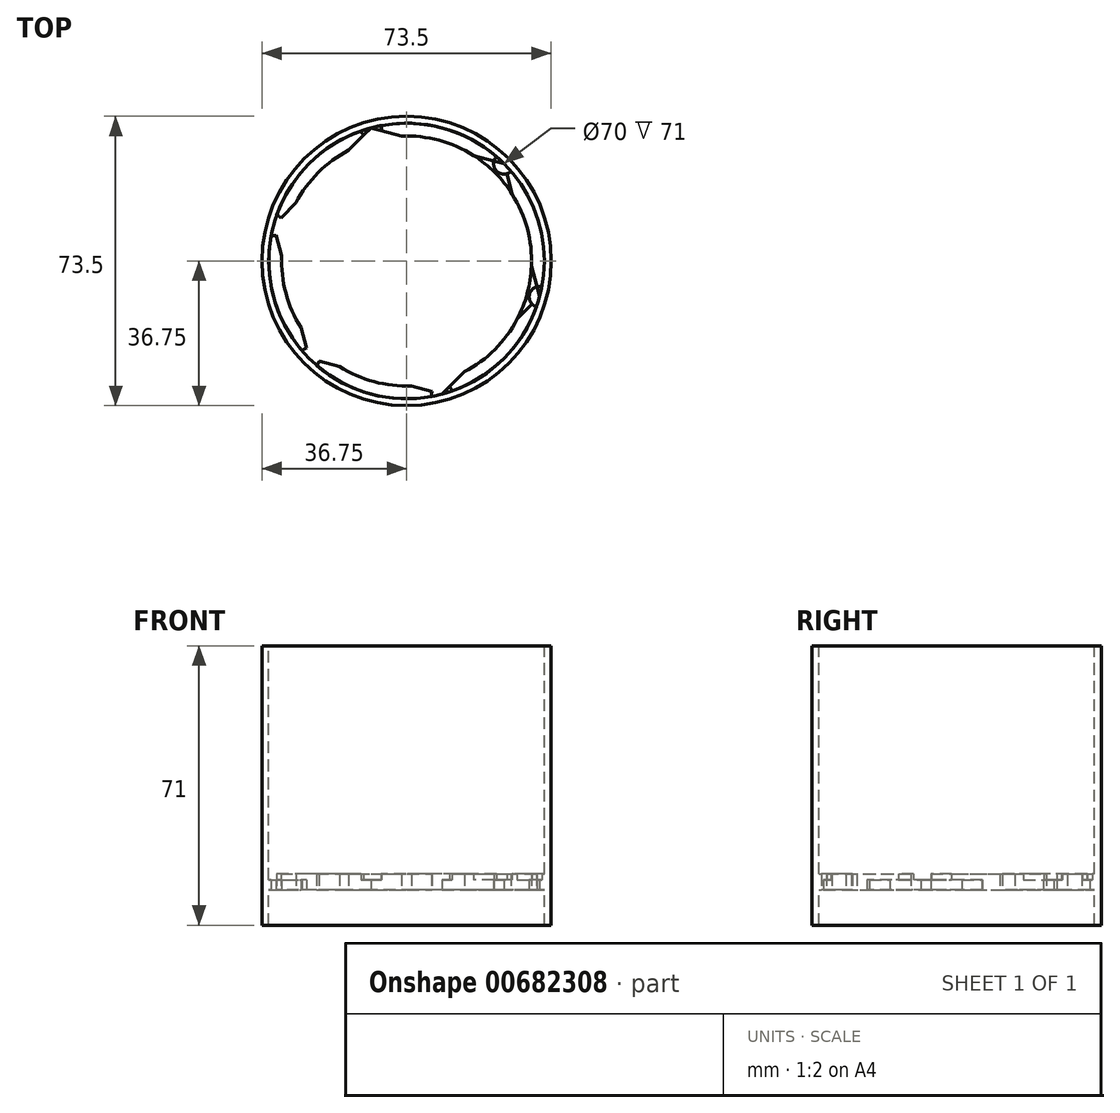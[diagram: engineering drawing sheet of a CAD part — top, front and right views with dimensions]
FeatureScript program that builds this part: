
annotation { "Feature Type Name" : "Feature", "Feature Type Description" : "" }
export const myFeature = defineFeature(function(context is Context, id is Id, definition is map)
    precondition{}
    {
        {
            var Q0;
            Q0=qCreatedBy(makeId("Top.planeOp"),FACE);
            var sketch = newSketch(context, id + "F0", { "sketchPlane" : qUnion([Q0])});
            skCircle(sketch, "E0", {"center": v(0, 0) * mm, "radius": 35 * mm});
            skCircle(sketch, "E1", {"center": v(0, 0) * mm, "radius": 36.75 * mm});
            skCircle(sketch, "E2", {"center": v(0, 0) * mm, "radius": 31.75 * mm});
            skCircle(sketch, "E3.cCircle", {"center": v(0, 0) * mm, "radius": 35 * mm, "construction": true});
            skLineSegment(sketch, "E3.0", {"start": v(-33.8, 9.1) * mm, "end": v(-9.02, 33.82) * mm});
            skLineSegment(sketch, "E3.1", {"start": v(-9.02, 33.82) * mm, "end": v(24.77, 24.72) * mm});
            skLineSegment(sketch, "E3.2", {"start": v(24.77, 24.72) * mm, "end": v(33.8, -9.1) * mm});
            skLineSegment(sketch, "E3.3", {"start": v(33.8, -9.1) * mm, "end": v(9.02, -33.82) * mm});
            skLineSegment(sketch, "E3.4", {"start": v(9.02, -33.82) * mm, "end": v(-24.77, -24.72) * mm});
            skLineSegment(sketch, "E3.5", {"start": v(-24.77, -24.72) * mm, "end": v(-33.8, 9.1) * mm});
            skArc(sketch, "E4", {"start": v(-6.44, 34.4) * mm, "mid": v(-8.34, 31.26) * mm, "end": v(-11.56, 33.04) * mm});
            skArc(sketch, "E5", {"start": v(26.57, 22.78) * mm, "mid": v(22.9, 22.85) * mm, "end": v(22.83, 26.53) * mm});
            skArc(sketch, "E6", {"start": v(33.01, -11.62) * mm, "mid": v(31.24, -8.4) * mm, "end": v(34.39, -6.5) * mm});
            skArc(sketch, "E7", {"start": v(6.44, -34.4) * mm, "mid": v(8.34, -31.26) * mm, "end": v(11.56, -33.04) * mm});
            skArc(sketch, "E8", {"start": v(-26.57, -22.78) * mm, "mid": v(-22.9, -22.85) * mm, "end": v(-22.83, -26.53) * mm});
            skArc(sketch, "E9", {"start": v(-33.01, 11.62) * mm, "mid": v(-31.24, 8.4) * mm, "end": v(-34.39, 6.5) * mm});
            skSolve(sketch);
        }
        {
            var Q0;
            Q0=makeQuery(id+"F0.imprint","IMPRINT",FACE,{"disambiguationData":[TD([[makeQuery(id+"F0.imprint","IMPRINT",EDGE,{"derivedFrom":sQuery(id+"F0.wireOp",EDGE,"E1")}),1.0]])]});
            extrude(context, id + "F1", {"entities" : qUnion([Q0]), "oppositeDirection" : true, "depth" : 9 * mm, "offsetDistance" : 25 * mm});
        }
        {
            var Q0;
            Q0=makeQuery(id+"F0.imprint","IMPRINT",FACE,{"disambiguationData":[TD([[makeQuery(id+"F0.imprint","IMPRINT",EDGE,{"derivedFrom":sQuery(id+"F0.wireOp",EDGE,"E1")}),1.0]])]});
            extrude(context, id + "F2", {"entities" : qUnion([Q0]), "operationType" : NewBodyOperationType.ADD, "depth" : 62 * mm, "offsetDistance" : 25 * mm});
        }
        {
            var Q0;
            {var subQ5=sQuery(id+"F0.wireOp",EDGE,"E0");var subQ8=sQuery(id+"F0.wireOp",EDGE,"E4");var subQ10=makeQuery(id+"F0.imprint","INTERSECT",VERTEX,{"disambiguationData":[OD(1.0)],"derivedFrom":[subQ5,subQ8]});Q0=makeQuery(id+"F0.imprint","IMPRINT",FACE,{"disambiguationData":[TD([[makeQuery(id+"F0.imprint","IMPRINT",EDGE,{"disambiguationData":[TD([[subQ10,-1.0]])],"derivedFrom":subQ5}),1.0]])]});}
            var Q1;
            {var subQ0=sQuery(id+"F0.wireOp",EDGE,"E3.0");var subQ1=sQuery(id+"F0.wireOp",EDGE,"E2");var subQ2=makeQuery(id+"F0.imprint","INTERSECT",VERTEX,{"disambiguationData":[OD(1.0)],"derivedFrom":[subQ1,subQ0]});Q1=makeQuery(id+"F0.imprint","IMPRINT",FACE,{"disambiguationData":[TD([[makeQuery(id+"F0.imprint","IMPRINT",EDGE,{"disambiguationData":[TD([[subQ2,-1.0]])],"derivedFrom":subQ1}),-1.0]])]});}
            var Q2;
            {var subQ6=sQuery(id+"F0.wireOp",EDGE,"E8");var subQ8=sQuery(id+"F0.wireOp",EDGE,"E0");var subQ9=makeQuery(id+"F0.imprint","INTERSECT",VERTEX,{"disambiguationData":[OD(0.0)],"derivedFrom":[subQ8,subQ6]});Q2=makeQuery(id+"F0.imprint","IMPRINT",FACE,{"disambiguationData":[TD([[makeQuery(id+"F0.imprint","IMPRINT",EDGE,{"disambiguationData":[TD([[subQ9,1.0]])],"derivedFrom":subQ8}),1.0]])]});}
            var Q3;
            {var subQ1=sQuery(id+"F0.wireOp",EDGE,"E3.0");var subQ3=sQuery(id+"F0.wireOp",EDGE,"E9");var subQ4=makeQuery(id+"F0.imprint","INTERSECT",VERTEX,{"derivedFrom":[subQ1,subQ3]});Q3=makeQuery(id+"F0.imprint","IMPRINT",FACE,{"disambiguationData":[TD([[makeQuery(id+"F0.imprint","IMPRINT",EDGE,{"disambiguationData":[TD([[subQ4,-1.0]])],"derivedFrom":subQ3}),-1.0]])]});}
            var Q4;
            {var subQ1=sQuery(id+"F0.wireOp",EDGE,"E0");var subQ3=sQuery(id+"F0.wireOp",EDGE,"E9");var subQ4=makeQuery(id+"F0.imprint","INTERSECT",VERTEX,{"disambiguationData":[OD(0.0)],"derivedFrom":[subQ1,subQ3]});Q4=makeQuery(id+"F0.imprint","IMPRINT",FACE,{"disambiguationData":[TD([[makeQuery(id+"F0.imprint","IMPRINT",EDGE,{"disambiguationData":[TD([[subQ4,-1.0]])],"derivedFrom":subQ3}),-1.0]])]});}
            var Q5;
            {var subQ1=sQuery(id+"F0.wireOp",EDGE,"E0");var subQ3=sQuery(id+"F0.wireOp",EDGE,"E9");var subQ4=makeQuery(id+"F0.imprint","INTERSECT",VERTEX,{"disambiguationData":[OD(1.0)],"derivedFrom":[subQ1,subQ3]});Q5=makeQuery(id+"F0.imprint","IMPRINT",FACE,{"disambiguationData":[TD([[makeQuery(id+"F0.imprint","IMPRINT",EDGE,{"disambiguationData":[TD([[subQ4,1.0]])],"derivedFrom":subQ3}),-1.0]])]});}
            var Q6;
            {var subQ0=sQuery(id+"F0.wireOp",EDGE,"E3.5");var subQ1=sQuery(id+"F0.wireOp",EDGE,"E2");var subQ2=makeQuery(id+"F0.imprint","INTERSECT",VERTEX,{"disambiguationData":[OD(1.0)],"derivedFrom":[subQ1,subQ0]});Q6=makeQuery(id+"F0.imprint","IMPRINT",FACE,{"disambiguationData":[TD([[makeQuery(id+"F0.imprint","IMPRINT",EDGE,{"disambiguationData":[TD([[subQ2,-1.0]])],"derivedFrom":subQ1}),-1.0]])]});}
            var Q7;
            Q7=makeQuery(id+"F0.imprint","IMPRINT",FACE,{"disambiguationData":[TD([[makeQuery(id+"F0.imprint","IMPRINT",EDGE,{"derivedFrom":sQuery(id+"F0.wireOp",EDGE,"yZACQcL7-3FR9-Hpo4-Rt52-3T5EJ3K1hziJ")}),-1.0]])]});
            var Q8;
            {var subQ5=sQuery(id+"F0.wireOp",EDGE,"E7");var subQ6=sQuery(id+"F0.wireOp",EDGE,"E0");var subQ7=makeQuery(id+"F0.imprint","INTERSECT",VERTEX,{"disambiguationData":[OD(0.0)],"derivedFrom":[subQ6,subQ5]});Q8=makeQuery(id+"F0.imprint","IMPRINT",FACE,{"disambiguationData":[TD([[makeQuery(id+"F0.imprint","IMPRINT",EDGE,{"disambiguationData":[TD([[subQ7,1.0]])],"derivedFrom":subQ6}),1.0]])]});}
            var Q9;
            {var subQ1=sQuery(id+"F0.wireOp",EDGE,"E3.4");var subQ3=sQuery(id+"F0.wireOp",EDGE,"E8");var subQ4=makeQuery(id+"F0.imprint","INTERSECT",VERTEX,{"derivedFrom":[subQ1,subQ3]});Q9=makeQuery(id+"F0.imprint","IMPRINT",FACE,{"disambiguationData":[TD([[makeQuery(id+"F0.imprint","IMPRINT",EDGE,{"disambiguationData":[TD([[subQ4,1.0]])],"derivedFrom":subQ3}),-1.0]])]});}
            var Q10;
            {var subQ1=sQuery(id+"F0.wireOp",EDGE,"E0");var subQ3=sQuery(id+"F0.wireOp",EDGE,"E8");var subQ4=makeQuery(id+"F0.imprint","INTERSECT",VERTEX,{"disambiguationData":[OD(1.0)],"derivedFrom":[subQ1,subQ3]});Q10=makeQuery(id+"F0.imprint","IMPRINT",FACE,{"disambiguationData":[TD([[makeQuery(id+"F0.imprint","IMPRINT",EDGE,{"disambiguationData":[TD([[subQ4,1.0]])],"derivedFrom":subQ3}),-1.0]])]});}
            var Q11;
            {var subQ1=sQuery(id+"F0.wireOp",EDGE,"E0");var subQ3=sQuery(id+"F0.wireOp",EDGE,"E8");var subQ4=makeQuery(id+"F0.imprint","INTERSECT",VERTEX,{"disambiguationData":[OD(0.0)],"derivedFrom":[subQ1,subQ3]});Q11=makeQuery(id+"F0.imprint","IMPRINT",FACE,{"disambiguationData":[TD([[makeQuery(id+"F0.imprint","IMPRINT",EDGE,{"disambiguationData":[TD([[subQ4,-1.0]])],"derivedFrom":subQ3}),-1.0]])]});}
            var Q12;
            {var subQ0=sQuery(id+"F0.wireOp",EDGE,"E3.4");var subQ1=sQuery(id+"F0.wireOp",EDGE,"E2");var subQ2=makeQuery(id+"F0.imprint","INTERSECT",VERTEX,{"disambiguationData":[OD(1.0)],"derivedFrom":[subQ1,subQ0]});Q12=makeQuery(id+"F0.imprint","IMPRINT",FACE,{"disambiguationData":[TD([[makeQuery(id+"F0.imprint","IMPRINT",EDGE,{"disambiguationData":[TD([[subQ2,-1.0]])],"derivedFrom":subQ1}),-1.0]])]});}
            var Q13;
            {var subQ1=sQuery(id+"F0.wireOp",EDGE,"E0");var subQ3=sQuery(id+"F0.wireOp",EDGE,"E7");var subQ4=makeQuery(id+"F0.imprint","INTERSECT",VERTEX,{"disambiguationData":[OD(0.0)],"derivedFrom":[subQ1,subQ3]});Q13=makeQuery(id+"F0.imprint","IMPRINT",FACE,{"disambiguationData":[TD([[makeQuery(id+"F0.imprint","IMPRINT",EDGE,{"disambiguationData":[TD([[subQ4,-1.0]])],"derivedFrom":subQ3}),-1.0]])]});}
            var Q14;
            {var subQ1=sQuery(id+"F0.wireOp",EDGE,"E3.3");var subQ3=sQuery(id+"F0.wireOp",EDGE,"E7");var subQ4=makeQuery(id+"F0.imprint","INTERSECT",VERTEX,{"derivedFrom":[subQ1,subQ3]});Q14=makeQuery(id+"F0.imprint","IMPRINT",FACE,{"disambiguationData":[TD([[makeQuery(id+"F0.imprint","IMPRINT",EDGE,{"disambiguationData":[TD([[subQ4,1.0]])],"derivedFrom":subQ3}),-1.0]])]});}
            var Q15;
            {var subQ1=sQuery(id+"F0.wireOp",EDGE,"E0");var subQ3=sQuery(id+"F0.wireOp",EDGE,"E7");var subQ4=makeQuery(id+"F0.imprint","INTERSECT",VERTEX,{"disambiguationData":[OD(1.0)],"derivedFrom":[subQ1,subQ3]});Q15=makeQuery(id+"F0.imprint","IMPRINT",FACE,{"disambiguationData":[TD([[makeQuery(id+"F0.imprint","IMPRINT",EDGE,{"disambiguationData":[TD([[subQ4,1.0]])],"derivedFrom":subQ3}),-1.0]])]});}
            var Q16;
            {var subQ3=sQuery(id+"F0.wireOp",EDGE,"E6");var subQ8=sQuery(id+"F0.wireOp",EDGE,"E0");var subQ9=makeQuery(id+"F0.imprint","INTERSECT",VERTEX,{"disambiguationData":[OD(0.0)],"derivedFrom":[subQ8,subQ3]});Q16=makeQuery(id+"F0.imprint","IMPRINT",FACE,{"disambiguationData":[TD([[makeQuery(id+"F0.imprint","IMPRINT",EDGE,{"disambiguationData":[TD([[subQ9,1.0]])],"derivedFrom":subQ8}),1.0]])]});}
            var Q17;
            {var subQ0=sQuery(id+"F0.wireOp",EDGE,"E3.2");var subQ1=sQuery(id+"F0.wireOp",EDGE,"E2");var subQ2=makeQuery(id+"F0.imprint","INTERSECT",VERTEX,{"disambiguationData":[OD(1.0)],"derivedFrom":[subQ1,subQ0]});Q17=makeQuery(id+"F0.imprint","IMPRINT",FACE,{"disambiguationData":[TD([[makeQuery(id+"F0.imprint","IMPRINT",EDGE,{"disambiguationData":[TD([[subQ2,1.0]])],"derivedFrom":subQ1}),-1.0]])]});}
            var Q18;
            {var subQ1=sQuery(id+"F0.wireOp",EDGE,"E3.2");var subQ3=sQuery(id+"F0.wireOp",EDGE,"E6");var subQ4=makeQuery(id+"F0.imprint","INTERSECT",VERTEX,{"derivedFrom":[subQ1,subQ3]});Q18=makeQuery(id+"F0.imprint","IMPRINT",FACE,{"disambiguationData":[TD([[makeQuery(id+"F0.imprint","IMPRINT",EDGE,{"disambiguationData":[TD([[subQ4,1.0]])],"derivedFrom":subQ3}),-1.0]])]});}
            var Q19;
            {var subQ1=sQuery(id+"F0.wireOp",EDGE,"E0");var subQ3=sQuery(id+"F0.wireOp",EDGE,"E6");var subQ4=makeQuery(id+"F0.imprint","INTERSECT",VERTEX,{"disambiguationData":[OD(0.0)],"derivedFrom":[subQ1,subQ3]});Q19=makeQuery(id+"F0.imprint","IMPRINT",FACE,{"disambiguationData":[TD([[makeQuery(id+"F0.imprint","IMPRINT",EDGE,{"disambiguationData":[TD([[subQ4,-1.0]])],"derivedFrom":subQ3}),-1.0]])]});}
            var Q20;
            {var subQ1=sQuery(id+"F0.wireOp",EDGE,"E0");var subQ3=sQuery(id+"F0.wireOp",EDGE,"E6");var subQ4=makeQuery(id+"F0.imprint","INTERSECT",VERTEX,{"disambiguationData":[OD(1.0)],"derivedFrom":[subQ1,subQ3]});Q20=makeQuery(id+"F0.imprint","IMPRINT",FACE,{"disambiguationData":[TD([[makeQuery(id+"F0.imprint","IMPRINT",EDGE,{"disambiguationData":[TD([[subQ4,1.0]])],"derivedFrom":subQ3}),-1.0]])]});}
            var Q21;
            {var subQ3=sQuery(id+"F0.wireOp",EDGE,"E5");var subQ5=sQuery(id+"F0.wireOp",EDGE,"E0");var subQ6=makeQuery(id+"F0.imprint","INTERSECT",VERTEX,{"disambiguationData":[OD(0.0)],"derivedFrom":[subQ5,subQ3]});Q21=makeQuery(id+"F0.imprint","IMPRINT",FACE,{"disambiguationData":[TD([[makeQuery(id+"F0.imprint","IMPRINT",EDGE,{"disambiguationData":[TD([[subQ6,1.0]])],"derivedFrom":subQ5}),1.0]])]});}
            var Q22;
            {var subQ0=sQuery(id+"F0.wireOp",EDGE,"E3.2");var subQ1=sQuery(id+"F0.wireOp",EDGE,"E2");var subQ2=makeQuery(id+"F0.imprint","INTERSECT",VERTEX,{"disambiguationData":[OD(0.0)],"derivedFrom":[subQ1,subQ0]});Q22=makeQuery(id+"F0.imprint","IMPRINT",FACE,{"disambiguationData":[TD([[makeQuery(id+"F0.imprint","IMPRINT",EDGE,{"disambiguationData":[TD([[subQ2,-1.0]])],"derivedFrom":subQ1}),-1.0]])]});}
            var Q23;
            {var subQ1=sQuery(id+"F0.wireOp",EDGE,"E3.1");var subQ3=sQuery(id+"F0.wireOp",EDGE,"E5");var subQ4=makeQuery(id+"F0.imprint","INTERSECT",VERTEX,{"derivedFrom":[subQ1,subQ3]});Q23=makeQuery(id+"F0.imprint","IMPRINT",FACE,{"disambiguationData":[TD([[makeQuery(id+"F0.imprint","IMPRINT",EDGE,{"disambiguationData":[TD([[subQ4,1.0]])],"derivedFrom":subQ3}),-1.0]])]});}
            var Q24;
            {var subQ1=sQuery(id+"F0.wireOp",EDGE,"E0");var subQ3=sQuery(id+"F0.wireOp",EDGE,"E5");var subQ4=makeQuery(id+"F0.imprint","INTERSECT",VERTEX,{"disambiguationData":[OD(0.0)],"derivedFrom":[subQ1,subQ3]});Q24=makeQuery(id+"F0.imprint","IMPRINT",FACE,{"disambiguationData":[TD([[makeQuery(id+"F0.imprint","IMPRINT",EDGE,{"disambiguationData":[TD([[subQ4,-1.0]])],"derivedFrom":subQ3}),-1.0]])]});}
            var Q25;
            {var subQ1=sQuery(id+"F0.wireOp",EDGE,"E0");var subQ3=sQuery(id+"F0.wireOp",EDGE,"E5");var subQ4=makeQuery(id+"F0.imprint","INTERSECT",VERTEX,{"disambiguationData":[OD(1.0)],"derivedFrom":[subQ1,subQ3]});Q25=makeQuery(id+"F0.imprint","IMPRINT",FACE,{"disambiguationData":[TD([[makeQuery(id+"F0.imprint","IMPRINT",EDGE,{"disambiguationData":[TD([[subQ4,1.0]])],"derivedFrom":subQ3}),-1.0]])]});}
            var Q26;
            {var subQ5=sQuery(id+"F0.wireOp",EDGE,"E4");var subQ6=sQuery(id+"F0.wireOp",EDGE,"E0");var subQ7=makeQuery(id+"F0.imprint","INTERSECT",VERTEX,{"disambiguationData":[OD(0.0)],"derivedFrom":[subQ6,subQ5]});Q26=makeQuery(id+"F0.imprint","IMPRINT",FACE,{"disambiguationData":[TD([[makeQuery(id+"F0.imprint","IMPRINT",EDGE,{"disambiguationData":[TD([[subQ7,1.0]])],"derivedFrom":subQ6}),1.0]])]});}
            var Q27;
            {var subQ0=sQuery(id+"F0.wireOp",EDGE,"E3.1");var subQ1=sQuery(id+"F0.wireOp",EDGE,"E2");var subQ2=makeQuery(id+"F0.imprint","INTERSECT",VERTEX,{"disambiguationData":[OD(1.0)],"derivedFrom":[subQ1,subQ0]});Q27=makeQuery(id+"F0.imprint","IMPRINT",FACE,{"disambiguationData":[TD([[makeQuery(id+"F0.imprint","IMPRINT",EDGE,{"disambiguationData":[TD([[subQ2,-1.0]])],"derivedFrom":subQ1}),-1.0]])]});}
            var Q28;
            {var subQ1=sQuery(id+"F0.wireOp",EDGE,"E3.0");var subQ3=sQuery(id+"F0.wireOp",EDGE,"E4");var subQ4=makeQuery(id+"F0.imprint","INTERSECT",VERTEX,{"derivedFrom":[subQ1,subQ3]});Q28=makeQuery(id+"F0.imprint","IMPRINT",FACE,{"disambiguationData":[TD([[makeQuery(id+"F0.imprint","IMPRINT",EDGE,{"disambiguationData":[TD([[subQ4,1.0]])],"derivedFrom":subQ3}),-1.0]])]});}
            var Q29;
            {var subQ1=sQuery(id+"F0.wireOp",EDGE,"E0");var subQ3=sQuery(id+"F0.wireOp",EDGE,"E4");var subQ4=makeQuery(id+"F0.imprint","INTERSECT",VERTEX,{"disambiguationData":[OD(1.0)],"derivedFrom":[subQ1,subQ3]});Q29=makeQuery(id+"F0.imprint","IMPRINT",FACE,{"disambiguationData":[TD([[makeQuery(id+"F0.imprint","IMPRINT",EDGE,{"disambiguationData":[TD([[subQ4,1.0]])],"derivedFrom":subQ3}),-1.0]])]});}
            var Q30;
            {var subQ1=sQuery(id+"F0.wireOp",EDGE,"E0");var subQ3=sQuery(id+"F0.wireOp",EDGE,"E4");var subQ4=makeQuery(id+"F0.imprint","INTERSECT",VERTEX,{"disambiguationData":[OD(0.0)],"derivedFrom":[subQ1,subQ3]});Q30=makeQuery(id+"F0.imprint","IMPRINT",FACE,{"disambiguationData":[TD([[makeQuery(id+"F0.imprint","IMPRINT",EDGE,{"disambiguationData":[TD([[subQ4,-1.0]])],"derivedFrom":subQ3}),-1.0]])]});}
            extrude(context, id + "F3", {"entities" : qUnion([Q0, Q1, Q2, Q3, Q4, Q5, Q6, Q7, Q8, Q9, Q10, Q11, Q12, Q13, Q14, Q15, Q16, Q17, Q18, Q19, Q20, Q21, Q22, Q23, Q24, Q25, Q26, Q27, Q28, Q29, Q30]), "operationType" : NewBodyOperationType.ADD, "depth" : 2.5 * mm, "offsetDistance" : 25 * mm});
        }
        {
            var Q0;
            {var subQ1=sQuery(id+"F0.wireOp",EDGE,"E3.3");var subQ3=sQuery(id+"F0.wireOp",EDGE,"E7");var subQ4=makeQuery(id+"F0.imprint","INTERSECT",VERTEX,{"derivedFrom":[subQ1,subQ3]});Q0=makeQuery(id+"F0.imprint","IMPRINT",FACE,{"disambiguationData":[TD([[makeQuery(id+"F0.imprint","IMPRINT",EDGE,{"disambiguationData":[TD([[subQ4,1.0]])],"derivedFrom":subQ3}),-1.0]])]});}
            var Q1;
            {var subQ1=sQuery(id+"F0.wireOp",EDGE,"E0");var subQ3=sQuery(id+"F0.wireOp",EDGE,"E7");var subQ4=makeQuery(id+"F0.imprint","INTERSECT",VERTEX,{"disambiguationData":[OD(1.0)],"derivedFrom":[subQ1,subQ3]});Q1=makeQuery(id+"F0.imprint","IMPRINT",FACE,{"disambiguationData":[TD([[makeQuery(id+"F0.imprint","IMPRINT",EDGE,{"disambiguationData":[TD([[subQ4,1.0]])],"derivedFrom":subQ3}),-1.0]])]});}
            var Q2;
            {var subQ1=sQuery(id+"F0.wireOp",EDGE,"E0");var subQ3=sQuery(id+"F0.wireOp",EDGE,"E7");var subQ4=makeQuery(id+"F0.imprint","INTERSECT",VERTEX,{"disambiguationData":[OD(0.0)],"derivedFrom":[subQ1,subQ3]});Q2=makeQuery(id+"F0.imprint","IMPRINT",FACE,{"disambiguationData":[TD([[makeQuery(id+"F0.imprint","IMPRINT",EDGE,{"disambiguationData":[TD([[subQ4,-1.0]])],"derivedFrom":subQ3}),-1.0]])]});}
            var Q3;
            {var subQ1=sQuery(id+"F0.wireOp",EDGE,"E0");var subQ3=sQuery(id+"F0.wireOp",EDGE,"E8");var subQ4=makeQuery(id+"F0.imprint","INTERSECT",VERTEX,{"disambiguationData":[OD(0.0)],"derivedFrom":[subQ1,subQ3]});Q3=makeQuery(id+"F0.imprint","IMPRINT",FACE,{"disambiguationData":[TD([[makeQuery(id+"F0.imprint","IMPRINT",EDGE,{"disambiguationData":[TD([[subQ4,-1.0]])],"derivedFrom":subQ3}),-1.0]])]});}
            var Q4;
            {var subQ1=sQuery(id+"F0.wireOp",EDGE,"E3.4");var subQ3=sQuery(id+"F0.wireOp",EDGE,"E8");var subQ4=makeQuery(id+"F0.imprint","INTERSECT",VERTEX,{"derivedFrom":[subQ1,subQ3]});Q4=makeQuery(id+"F0.imprint","IMPRINT",FACE,{"disambiguationData":[TD([[makeQuery(id+"F0.imprint","IMPRINT",EDGE,{"disambiguationData":[TD([[subQ4,1.0]])],"derivedFrom":subQ3}),-1.0]])]});}
            var Q5;
            {var subQ1=sQuery(id+"F0.wireOp",EDGE,"E0");var subQ3=sQuery(id+"F0.wireOp",EDGE,"E8");var subQ4=makeQuery(id+"F0.imprint","INTERSECT",VERTEX,{"disambiguationData":[OD(1.0)],"derivedFrom":[subQ1,subQ3]});Q5=makeQuery(id+"F0.imprint","IMPRINT",FACE,{"disambiguationData":[TD([[makeQuery(id+"F0.imprint","IMPRINT",EDGE,{"disambiguationData":[TD([[subQ4,1.0]])],"derivedFrom":subQ3}),-1.0]])]});}
            var Q6;
            {var subQ1=sQuery(id+"F0.wireOp",EDGE,"E0");var subQ3=sQuery(id+"F0.wireOp",EDGE,"E9");var subQ4=makeQuery(id+"F0.imprint","INTERSECT",VERTEX,{"disambiguationData":[OD(0.0)],"derivedFrom":[subQ1,subQ3]});Q6=makeQuery(id+"F0.imprint","IMPRINT",FACE,{"disambiguationData":[TD([[makeQuery(id+"F0.imprint","IMPRINT",EDGE,{"disambiguationData":[TD([[subQ4,-1.0]])],"derivedFrom":subQ3}),-1.0]])]});}
            var Q7;
            {var subQ1=sQuery(id+"F0.wireOp",EDGE,"E3.0");var subQ3=sQuery(id+"F0.wireOp",EDGE,"E9");var subQ4=makeQuery(id+"F0.imprint","INTERSECT",VERTEX,{"derivedFrom":[subQ1,subQ3]});Q7=makeQuery(id+"F0.imprint","IMPRINT",FACE,{"disambiguationData":[TD([[makeQuery(id+"F0.imprint","IMPRINT",EDGE,{"disambiguationData":[TD([[subQ4,-1.0]])],"derivedFrom":subQ3}),-1.0]])]});}
            var Q8;
            {var subQ1=sQuery(id+"F0.wireOp",EDGE,"E0");var subQ3=sQuery(id+"F0.wireOp",EDGE,"E9");var subQ4=makeQuery(id+"F0.imprint","INTERSECT",VERTEX,{"disambiguationData":[OD(1.0)],"derivedFrom":[subQ1,subQ3]});Q8=makeQuery(id+"F0.imprint","IMPRINT",FACE,{"disambiguationData":[TD([[makeQuery(id+"F0.imprint","IMPRINT",EDGE,{"disambiguationData":[TD([[subQ4,1.0]])],"derivedFrom":subQ3}),-1.0]])]});}
            var Q9;
            {var subQ1=sQuery(id+"F0.wireOp",EDGE,"E3.0");var subQ3=sQuery(id+"F0.wireOp",EDGE,"E4");var subQ4=makeQuery(id+"F0.imprint","INTERSECT",VERTEX,{"derivedFrom":[subQ1,subQ3]});Q9=makeQuery(id+"F0.imprint","IMPRINT",FACE,{"disambiguationData":[TD([[makeQuery(id+"F0.imprint","IMPRINT",EDGE,{"disambiguationData":[TD([[subQ4,1.0]])],"derivedFrom":subQ3}),-1.0]])]});}
            var Q10;
            {var subQ1=sQuery(id+"F0.wireOp",EDGE,"E0");var subQ3=sQuery(id+"F0.wireOp",EDGE,"E4");var subQ4=makeQuery(id+"F0.imprint","INTERSECT",VERTEX,{"disambiguationData":[OD(0.0)],"derivedFrom":[subQ1,subQ3]});Q10=makeQuery(id+"F0.imprint","IMPRINT",FACE,{"disambiguationData":[TD([[makeQuery(id+"F0.imprint","IMPRINT",EDGE,{"disambiguationData":[TD([[subQ4,-1.0]])],"derivedFrom":subQ3}),-1.0]])]});}
            var Q11;
            {var subQ1=sQuery(id+"F0.wireOp",EDGE,"E0");var subQ3=sQuery(id+"F0.wireOp",EDGE,"E4");var subQ4=makeQuery(id+"F0.imprint","INTERSECT",VERTEX,{"disambiguationData":[OD(1.0)],"derivedFrom":[subQ1,subQ3]});Q11=makeQuery(id+"F0.imprint","IMPRINT",FACE,{"disambiguationData":[TD([[makeQuery(id+"F0.imprint","IMPRINT",EDGE,{"disambiguationData":[TD([[subQ4,1.0]])],"derivedFrom":subQ3}),-1.0]])]});}
            var Q12;
            {var subQ1=sQuery(id+"F0.wireOp",EDGE,"E0");var subQ3=sQuery(id+"F0.wireOp",EDGE,"E5");var subQ4=makeQuery(id+"F0.imprint","INTERSECT",VERTEX,{"disambiguationData":[OD(1.0)],"derivedFrom":[subQ1,subQ3]});Q12=makeQuery(id+"F0.imprint","IMPRINT",FACE,{"disambiguationData":[TD([[makeQuery(id+"F0.imprint","IMPRINT",EDGE,{"disambiguationData":[TD([[subQ4,1.0]])],"derivedFrom":subQ3}),-1.0]])]});}
            var Q13;
            {var subQ1=sQuery(id+"F0.wireOp",EDGE,"E3.1");var subQ3=sQuery(id+"F0.wireOp",EDGE,"E5");var subQ4=makeQuery(id+"F0.imprint","INTERSECT",VERTEX,{"derivedFrom":[subQ1,subQ3]});Q13=makeQuery(id+"F0.imprint","IMPRINT",FACE,{"disambiguationData":[TD([[makeQuery(id+"F0.imprint","IMPRINT",EDGE,{"disambiguationData":[TD([[subQ4,1.0]])],"derivedFrom":subQ3}),-1.0]])]});}
            var Q14;
            {var subQ1=sQuery(id+"F0.wireOp",EDGE,"E0");var subQ3=sQuery(id+"F0.wireOp",EDGE,"E5");var subQ4=makeQuery(id+"F0.imprint","INTERSECT",VERTEX,{"disambiguationData":[OD(0.0)],"derivedFrom":[subQ1,subQ3]});Q14=makeQuery(id+"F0.imprint","IMPRINT",FACE,{"disambiguationData":[TD([[makeQuery(id+"F0.imprint","IMPRINT",EDGE,{"disambiguationData":[TD([[subQ4,-1.0]])],"derivedFrom":subQ3}),-1.0]])]});}
            var Q15;
            {var subQ1=sQuery(id+"F0.wireOp",EDGE,"E3.2");var subQ3=sQuery(id+"F0.wireOp",EDGE,"E6");var subQ4=makeQuery(id+"F0.imprint","INTERSECT",VERTEX,{"derivedFrom":[subQ1,subQ3]});Q15=makeQuery(id+"F0.imprint","IMPRINT",FACE,{"disambiguationData":[TD([[makeQuery(id+"F0.imprint","IMPRINT",EDGE,{"disambiguationData":[TD([[subQ4,1.0]])],"derivedFrom":subQ3}),-1.0]])]});}
            var Q16;
            {var subQ1=sQuery(id+"F0.wireOp",EDGE,"E0");var subQ3=sQuery(id+"F0.wireOp",EDGE,"E6");var subQ4=makeQuery(id+"F0.imprint","INTERSECT",VERTEX,{"disambiguationData":[OD(1.0)],"derivedFrom":[subQ1,subQ3]});Q16=makeQuery(id+"F0.imprint","IMPRINT",FACE,{"disambiguationData":[TD([[makeQuery(id+"F0.imprint","IMPRINT",EDGE,{"disambiguationData":[TD([[subQ4,1.0]])],"derivedFrom":subQ3}),-1.0]])]});}
            var Q17;
            {var subQ1=sQuery(id+"F0.wireOp",EDGE,"E0");var subQ3=sQuery(id+"F0.wireOp",EDGE,"E6");var subQ4=makeQuery(id+"F0.imprint","INTERSECT",VERTEX,{"disambiguationData":[OD(0.0)],"derivedFrom":[subQ1,subQ3]});Q17=makeQuery(id+"F0.imprint","IMPRINT",FACE,{"disambiguationData":[TD([[makeQuery(id+"F0.imprint","IMPRINT",EDGE,{"disambiguationData":[TD([[subQ4,-1.0]])],"derivedFrom":subQ3}),-1.0]])]});}
            extrude(context, id + "F4", {"entities" : qUnion([Q0, Q1, Q2, Q3, Q4, Q5, Q6, Q7, Q8, Q9, Q10, Q11, Q12, Q13, Q14, Q15, Q16, Q17]), "operationType" : NewBodyOperationType.ADD, "depth" : 4 * mm, "offsetDistance" : 25 * mm});
        }
    });
